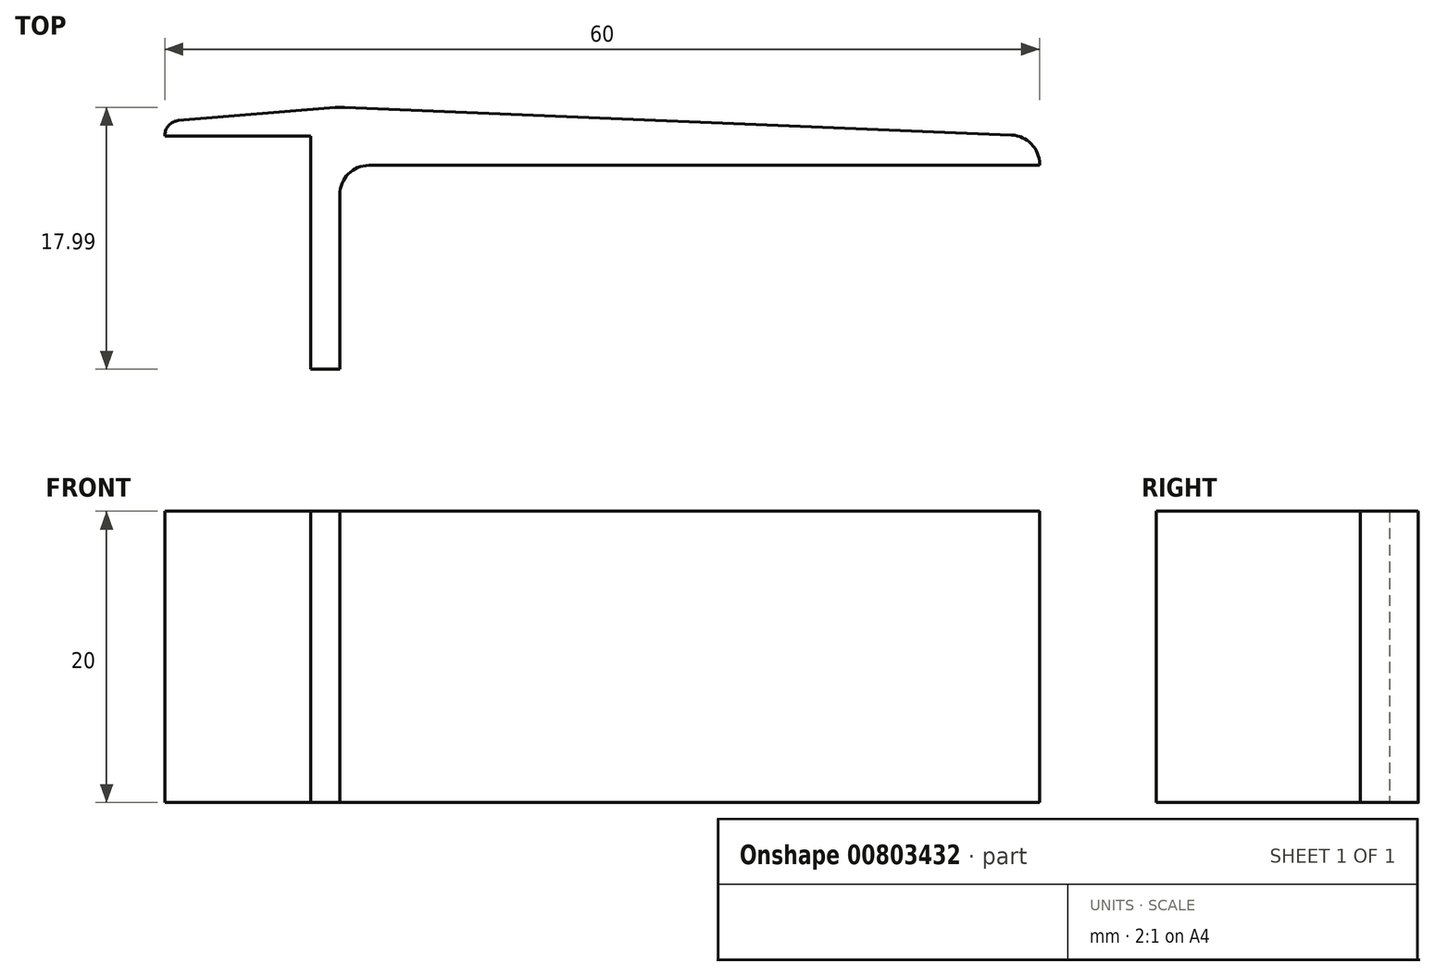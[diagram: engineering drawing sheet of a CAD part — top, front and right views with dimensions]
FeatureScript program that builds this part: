
annotation { "Feature Type Name" : "Feature", "Feature Type Description" : "" }
export const myFeature = defineFeature(function(context is Context, id is Id, definition is map)
    precondition{}
    {
        {
            var Q0;
            Q0=qCreatedBy(makeId("Top.planeOp"),FACE);
            var sketch = newSketch(context, id + "F0", { "sketchPlane" : qUnion([Q0])});
            skLineSegment(sketch, "E0", {"start": v(0, 0) * mm, "end": v(0, 16) * mm});
            skLineSegment(sketch, "E1", {"start": v(0, 16) * mm, "end": v(-10, 16) * mm});
            skLineSegment(sketch, "E2", {"start": v(0, 0) * mm, "end": v(2, 0) * mm});
            skPoint(sketch, "E3", {"position": v(2, 18) * mm});
            skLineSegment(sketch, "E4", {"start": v(2, 0) * mm, "end": v(2, 14) * mm});
            skLineSegment(sketch, "E5", {"start": v(2, 14) * mm, "end": v(50, 14) * mm});
            skLineSegment(sketch, "E6", {"start": v(50, 14) * mm, "end": v(50, 16) * mm});
            skLineSegment(sketch, "E7", {"start": v(50, 16) * mm, "end": v(2, 18) * mm});
            skLineSegment(sketch, "E8", {"start": v(-10, 16) * mm, "end": v(-10, 17) * mm});
            skLineSegment(sketch, "E9", {"start": v(-10, 17) * mm, "end": v(2, 18) * mm});
            skSolve(sketch);
        }
        {
            var Q0;
            Q0=makeQuery(id+"F0.imprint","IMPRINT",FACE,{"disambiguationData":[TD([[makeQuery(id+"F0.imprint","IMPRINT",EDGE,{"derivedFrom":sQuery(id+"F0.wireOp",EDGE,"E0")}),-1.0]])]});
            extrude(context, id + "F1", {"entities" : qUnion([Q0]), "depth" : 20 * mm, "offsetDistance" : 25 * mm});
        }
        {
            var Q0;
            Q0=makeQuery(id+"F1.opExtrude","SWEPT_EDGE",EDGE,{"disambiguationData":[OSD([sQuery(id+"F0.wireOp",EDGE,"E6"),sQuery(id+"F0.wireOp",EDGE,"E7")])]});
            var Q1;
            Q1=makeQuery(id+"F1.opExtrude","SWEPT_EDGE",EDGE,{"disambiguationData":[OSD([sQuery(id+"F0.wireOp",EDGE,"E4"),sQuery(id+"F0.wireOp",EDGE,"E5")])]});
            fillet(context, id + "F2", {"entities" : qUnion([Q0, Q1]), "radius" : 2 * mm, "tangentPropagation" : true, "allowEdgeOverflow" : false});
        }
        {
            var Q0;
            Q0=makeQuery(id+"F1.opExtrude","SWEPT_EDGE",EDGE,{"disambiguationData":[OSD([sQuery(id+"F0.wireOp",EDGE,"E8"),sQuery(id+"F0.wireOp",EDGE,"E9")])]});
            fillet(context, id + "F3", {"entities" : qUnion([Q0]), "radius" : 1 * mm, "tangentPropagation" : true, "allowEdgeOverflow" : false});
        }
        {
            var Q0;
            Q0=makeQuery(id+"F1.opExtrude","SWEPT_EDGE",EDGE,{"disambiguationData":[OSD([sQuery(id+"F0.wireOp",EDGE,"E7"),sQuery(id+"F0.wireOp",EDGE,"E9")])]});
            fillet(context, id + "F4", {"entities" : qUnion([Q0]), "radius" : 5 * mm, "tangentPropagation" : true, "allowEdgeOverflow" : false});
        }
    });
